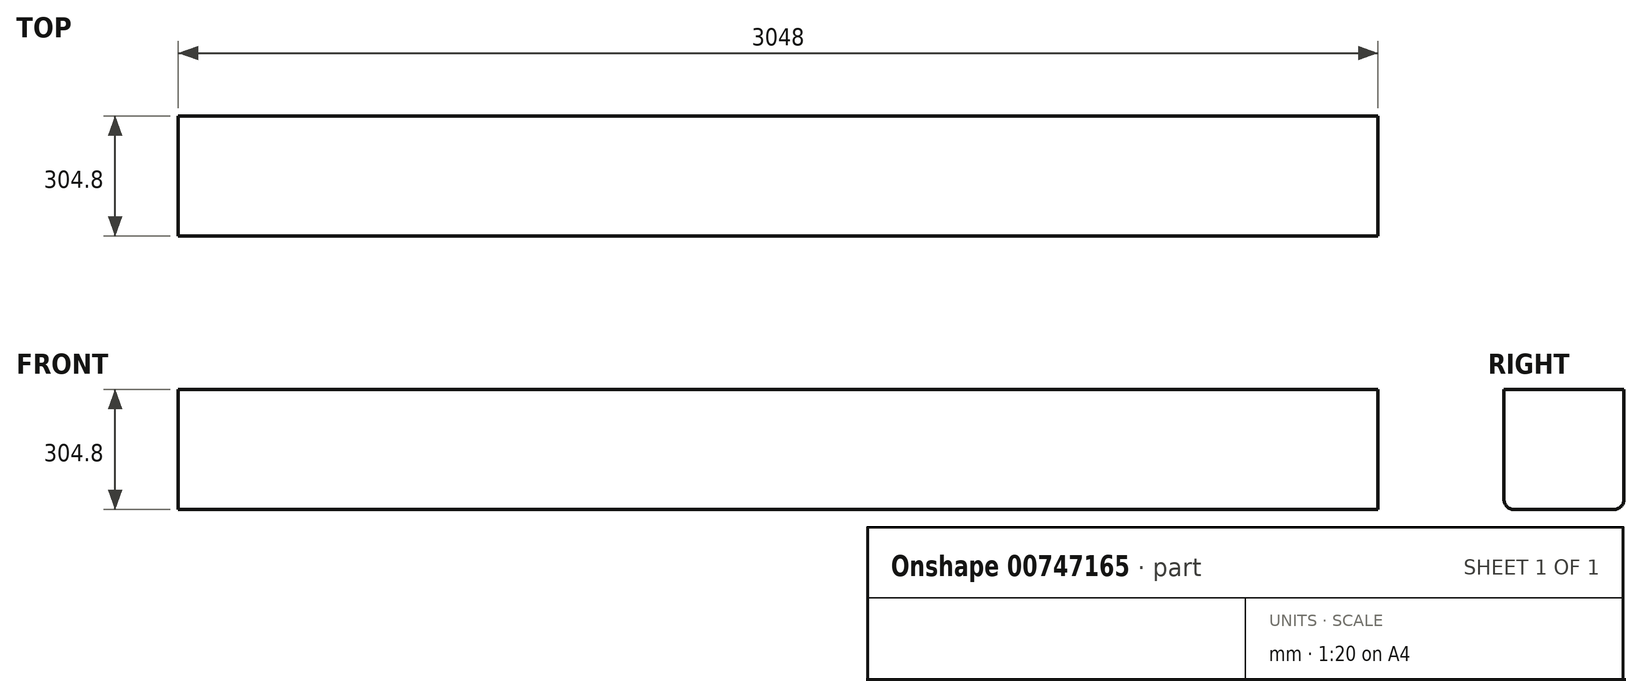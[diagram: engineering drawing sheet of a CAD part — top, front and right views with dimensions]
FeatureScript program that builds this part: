
annotation { "Feature Type Name" : "Feature", "Feature Type Description" : "" }
export const myFeature = defineFeature(function(context is Context, id is Id, definition is map)
    precondition{}
    {
        {
            var Q0;
            Q0=qCreatedBy(makeId("Right.planeOp"),FACE);
            var sketch = newSketch(context, id + "F0", { "sketchPlane" : qUnion([Q0])});
            skLineSegment(sketch, "E0.bottom", {"start": v(-183.01, 140.16) * mm, "end": v(121.79, 140.16) * mm});
            skLineSegment(sketch, "E0.top", {"start": v(-183.01, -164.64) * mm, "end": v(121.79, -164.64) * mm});
            skLineSegment(sketch, "E0.left", {"start": v(-183.01, 140.16) * mm, "end": v(-183.01, -164.64) * mm});
            skLineSegment(sketch, "E0.right", {"start": v(121.79, 140.16) * mm, "end": v(121.79, -164.64) * mm});
            skSolve(sketch);
        }
        {
            var Q0;
            Q0 = qSketchRegion(id + "F0", true);
            extrude(context, id + "F1", {"entities" : qUnion([Q0]), "depth" : 3048 * mm, "offsetDistance" : 25.4 * mm});
        }
        {
            var Q0;
            Q0=makeQuery(id+"F1.opExtrude","SWEPT_EDGE",EDGE,{"disambiguationData":[OSD([sQuery(id+"F0.wireOp",EDGE,"E0.top"),sQuery(id+"F0.wireOp",EDGE,"E0.left")])]});
            var Q1;
            Q1=makeQuery(id+"F1.opExtrude","SWEPT_EDGE",EDGE,{"disambiguationData":[OSD([sQuery(id+"F0.wireOp",EDGE,"E0.top"),sQuery(id+"F0.wireOp",EDGE,"E0.right")])]});
            fillet(context, id + "F2", {"entities" : qUnion([Q0, Q1]), "radius" : 25.4 * mm, "tangentPropagation" : true, "allowEdgeOverflow" : false});
        }
    });
